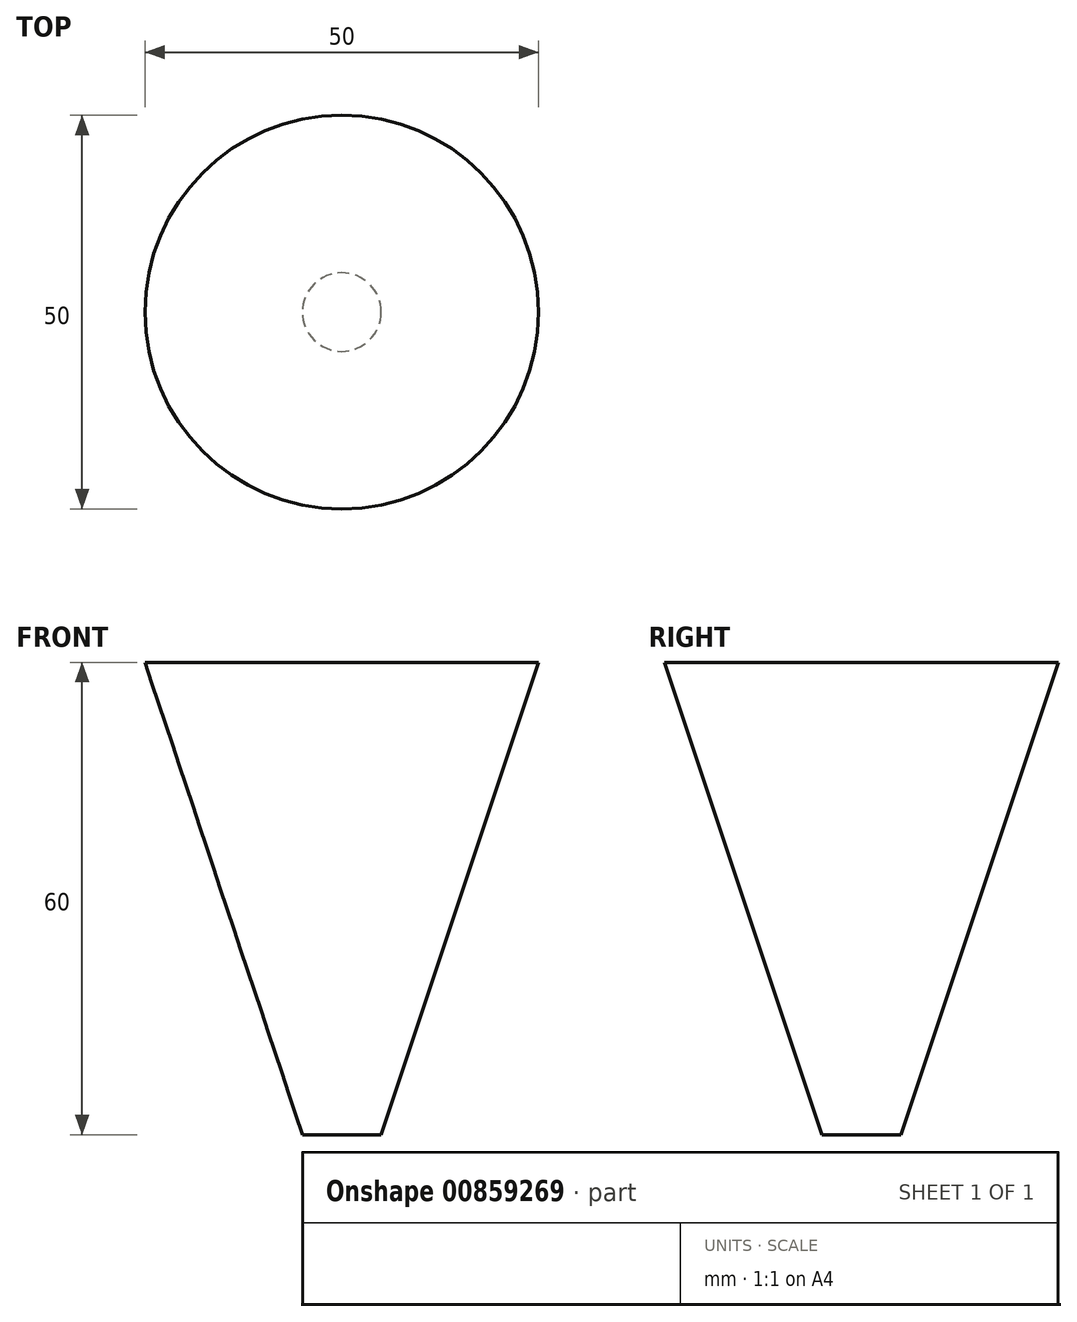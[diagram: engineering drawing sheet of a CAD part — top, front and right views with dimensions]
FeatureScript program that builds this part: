
annotation { "Feature Type Name" : "Feature", "Feature Type Description" : "" }
export const myFeature = defineFeature(function(context is Context, id is Id, definition is map)
    precondition{}
    {
        {
            var Q0;
            Q0=qCreatedBy(makeId("Front.planeOp"),FACE);
            var sketch = newSketch(context, id + "F0", { "sketchPlane" : qUnion([Q0])});
            skLineSegment(sketch, "E0", {"start": v(0, 0) * mm, "end": v(-5, 0) * mm});
            skLineSegment(sketch, "E1", {"start": v(0, 0) * mm, "end": v(0, 60) * mm});
            skLineSegment(sketch, "E2", {"start": v(0, 60) * mm, "end": v(-25, 60) * mm});
            skLineSegment(sketch, "E3", {"start": v(-25, 60) * mm, "end": v(-5, 0) * mm});
            skSolve(sketch);
        }
        {
            var Q0;
            Q0=makeQuery(id+"F0.imprint","IMPRINT",FACE,{"disambiguationData":[TD([[makeQuery(id+"F0.imprint","IMPRINT",EDGE,{"derivedFrom":sQuery(id+"F0.wireOp",EDGE,"E0")}),-1.0]])]});
            var Q1;
            Q1=sQuery(id+"F0.wireOp",EDGE,"E1");
            revolve(context, id + "F1", {"surfaceOperationType" : NewSurfaceOperationType.NEW, "entities" : qUnion([Q0]), "axis" : qUnion([Q1]), "revolveType" : RevolveType.FULL});
        }
    });
